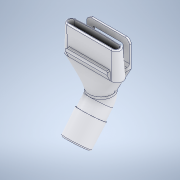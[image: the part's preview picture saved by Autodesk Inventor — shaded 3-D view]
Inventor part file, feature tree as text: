
AUTODESK INVENTOR PART (.ipt)
format: ipt  version: 2022 (Build 260153000, 153)  size: 1,091,584 bytes
history: native  units: in
note: dims shown in document units (in); Inventor stores cm internally (conversion verified against a paired STEP export)
features: sketch x13, extrude x7, loft x5, plane x4, other x4, fillet x3, sweep x2
ambient origin geometry x8: Origin, YZ Plane, XZ Plane, XY Plane, X Axis, Y Axis, Z Axis, Center Point
bodies: Solid1 (feature_tree), Solid3 (feature_tree)
feature tree (38):
  sketch  "Sketch1"  dims[d0=0.3543in d1=1.9016in]
  plane  "Work Plane1"
  sketch  "Sketch2"  dims[d2=0.3248in d3=0.0591in]
  loft  "Loft1"
  loft  "Loft2"
  plane  "Work Plane2"
  extrude  "Extrusion1"  Depth=0.4331in
  extrude  "Extrusion2"  Depth=0.4134in
  plane  "Work Plane3"
  extrude  "Extrusion3"  TaperAngle=0.0deg  [1 undecoded]
  loft  "Loft4"
  loft  "Loft6"
  fillet  "Fillet2"  Radius=0.0531in
  fillet  "Fillet3"  Radius=1.5157in
  extrude  "Extrusion5"  Depth=0.2165in
  extrude  "Extrusion6"  Depth=1.1024in
  sketch  "Sketch13"  dims[d22=1.063in d23=1.1024in]
  sketch  "Sketch12"  dims[d20=0.1575in d21=0.2165in]
  sweep  "Sweep1"
  sweep  "Sweep2"
  extrude  "Extrusion7"  Depth=0.8307in
  sketch  "Sketch17"  dims[d26=0.0669in d27=0.0in d28=0.1181in d29=0.0in]
  plane  "Work Plane6"
  loft  "Loft9"
  extrude  "Extrusion9"  TaperAngle=0.0deg  [1 undecoded]
  fillet  "Fillet5"  [1 undecoded]
  sketch  "Sketch3"  dims[d4=-0.9843in d5=0.4331in]
  sketch  "Sketch5"  dims[d6=1.9882in d7=0.4134in]
  sketch  "Sketch6"  dims[d8=0.0591in d9=0.0in d10=90.0deg]
  other  "Edges7"
  other  "Edges8"
  other  "Edges3"
  other  "Edges4"
  sketch  "Sketch10"  dims[d11=0.0in d12=90.0deg d13=0.0in d14=90.0deg]
  sketch  "Sketch11"  dims[d15=0.0in d16=90.0deg d17=-0.6693in d18=0.0531in d19=1.5157in]
  sketch  "Sketch14"  dims[d24=0.5197in d25=0.0394in]
  sketch  "Sketch18"  dims[d30=0.7874in d31=0.8307in]
  sketch  "Sketch19"  dims[d32=0.5276in d33=0.0787in d34=0.0in d39=0.0in d40=90.0deg d41=0.0in d42=90.0deg d47=0.0in d48=90.0deg d49=0.0in d50=90.0deg d62=0.0787in d63=0.0394in d64=0.6594in d66=1.4803in d67=0.1181in d68=0.0394in d69=0.0984in d70=0.0in d71=1.4764in d72=0.0in d75=0.2749in d76=0.0in d77=0.0in d78=0.0in d79=0.0in d80=0.3937in d81=0.0in d94=0.8819in d95=0.8268in d96=0.8598in d97=0.0in d98=90.0deg d99=0.0in d100=90.0deg d101=0.5276in d102=0.8268in d103=0.0in d104=0.0394in]
note: 3 required parameter values undecoded (feature->parameter linkage not recoverable at this tier; creation-order binding heuristic only, values carry confidence <= 0.55)
